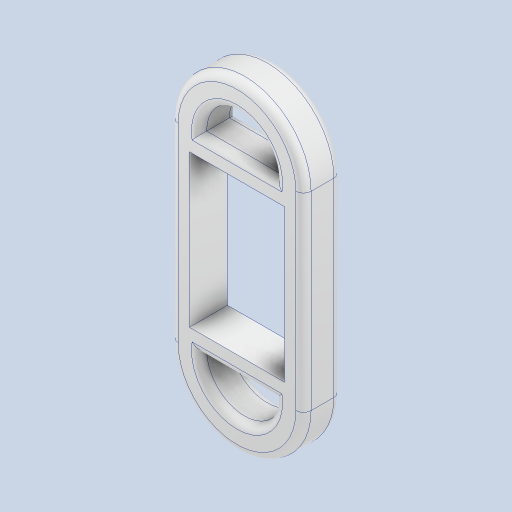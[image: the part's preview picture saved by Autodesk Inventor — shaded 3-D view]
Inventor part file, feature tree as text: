
AUTODESK INVENTOR PART (.ipt)
format: ipt  version: 2024 (Build 280153000, 153)  size: 237,568 bytes
history: native  units: mm
features: other x1, extrude x1, fillet x1, sketch x1
ambient origin geometry x8: Origin, YZ Plane, XZ Plane, XY Plane, X Axis, Y Axis, Z Axis, Center Point
bodies: Body1 (feature_tree)
feature tree (4):
  other  "Sólido1"
  extrude  "Extrusión1"  Depth=4.0mm
  fillet  "Empalme1"  Radius=15.0mm
  sketch  "Boceto1"  dims[d0=170.0mm d1=70.0mm d2=15.0mm d3=20.0mm d4=40.0mm d6=80.0mm d7=10.0mm d8=10.0mm d9=20.0mm d10=0.0mm d11=4.0mm]
